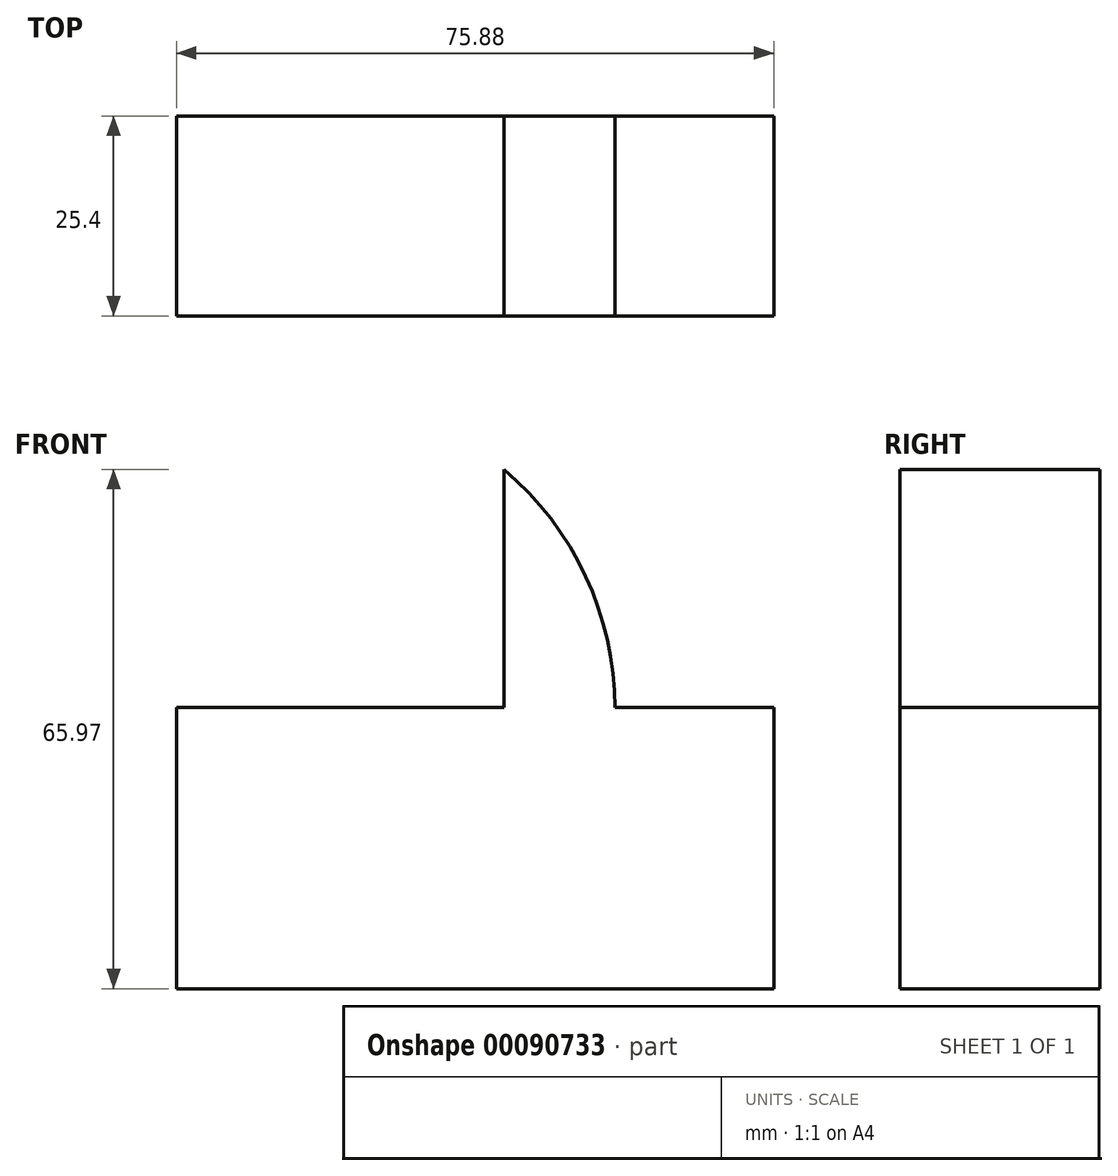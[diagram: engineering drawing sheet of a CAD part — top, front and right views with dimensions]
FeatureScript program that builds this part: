
annotation { "Feature Type Name" : "Feature", "Feature Type Description" : "" }
export const myFeature = defineFeature(function(context is Context, id is Id, definition is map)
    precondition{}
    {
        {
            var Q0;
            Q0=qCreatedBy(makeId("Front.planeOp"),FACE);
            var sketch = newSketch(context, id + "F0", { "sketchPlane" : qUnion([Q0])});
            skLineSegment(sketch, "E0.bottom", {"start": v(-41.6, 12.08) * mm, "end": v(34.29, 12.08) * mm});
            skLineSegment(sketch, "E0.top", {"start": v(-41.6, -23.6) * mm, "end": v(34.29, -23.6) * mm});
            skLineSegment(sketch, "E0.left", {"start": v(-41.6, 12.08) * mm, "end": v(-41.6, -23.6) * mm});
            skLineSegment(sketch, "E0.right", {"start": v(34.29, 12.08) * mm, "end": v(34.29, -23.6) * mm});
            skArc(sketch, "E1", {"start": v(0, 42.36) * mm, "mid": v(10.4, 28.78) * mm, "end": v(14.08, 12.08) * mm});
            skLineSegment(sketch, "E2", {"start": v(0, 42.36) * mm, "end": v(0, 12.08) * mm});
            skSolve(sketch);
        }
        {
            var Q0;
            Q0 = qSketchRegion(id + "F0", true);
            extrude(context, id + "F1", {"entities" : qUnion([Q0]), "depth" : 25.4 * mm});
        }
    });
